# Revit family: 318_41de1b6ba8b346a1a332b3068bab22
name_source: partatom
category: Pipe Accessories
units: mm (PartAtom-declared; Revit-internal decimal feet)

## family parameters
Always vertical = Yes
Cut with Voids When Loaded = No
Part Type = Valve - Normal
Round Connector Dimension = Use Diameter
Shared = No
Work Plane-Based = No

## types (1)
- Manifold SL 1” - 10 Circuits
    BO1 = 102 mm  [stored 0.334646 ft]
    BV1 = No
    CXIO1 = 17 mm  [stored 0.0557743 ft]
    CXO1 = 50 mm  [stored 0.164042 ft]
    DBB2 = 400 mm  [stored 1.31234 ft]
    Description = Manifold SL 1” - 10 Circuits - Material: PA6.6+Glass fiber
    L_2 = 302 mm
    MC Product Code = Manifold SL 1” - 10 Circuits
    MP1 = 32 mm
    MP3 = 32 mm
    Manufacturer = Eurotherm
    QmdConnectorList = 321;MP1;322;SPD1;323;SPD2;324;SPD3;325;SPD4;326;SPD5;327;SPD6;328;SPD7;329;SPD8;330;SPD9;331;SPD10;351;MP3;352;RPD1;353;RPD2;354;RPD3;355;RPD4;356;RPD5;357;RPD6;358;RPD7;359;RPD8;360;RPD9;361;RPD10
    RPD1 = 20 mm
    RPD10 = 20 mm
    RPD2 = 20 mm
    RPD3 = 20 mm
    RPD4 = 20 mm
    RPD5 = 20 mm
    RPD6 = 20 mm
    RPD7 = 20 mm
    RPD8 = 20 mm
    RPD9 = 20 mm
    RYO1 = 52 mm  [stored 0.170604 ft]
    RZO1 = 63 mm
    SCO1 = 2 mm  [stored 0.00656168 ft]
    SMH1_ = 27 mm  [stored 0.0885827 ft]
    SML1 = 500 mm  [stored 1.64042 ft]
    SMR1 = 23 mm  [stored 0.0754593 ft]
    SMW1 = 50 mm  [stored 0.164042 ft]
    SMW1_ = 25 mm  [stored 0.082021 ft]
    SMW1__ve = -50 mm  [stored -0.164042 ft]
    SPD1 = 20 mm
    SPD10 = 20 mm
    SPD2 = 20 mm
    SPD3 = 20 mm
    SPD4 = 20 mm
    SPD5 = 20 mm
    SPD6 = 20 mm
    SPD7 = 20 mm
    SPD8 = 20 mm
    SPD9 = 20 mm
    STL1 = 59 mm
    SYO1 = 36 mm
    SZO1 = 273 mm
    TH_2 = 177 mm
    URL = https://www.eurotherm.info
    magiPartTypeId = 318
    magiProductFamilyId = 41de1b6ba8b346a1a332b3068bab22
    magiProductId = 41de1b6ba8b346a1a332b3068bab22

note: [stored X ft] marks values corroborated as IEEE doubles in the binary element streams (Revit-internal decimal feet)

## geometry (parser evidence)
native form markers: Sweep x2
no freeform markers — native parametric forms only
